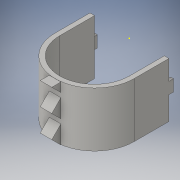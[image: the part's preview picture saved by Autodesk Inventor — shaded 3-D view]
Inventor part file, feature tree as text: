
AUTODESK INVENTOR PART (.ipt)
format: ipt  version: 2016 (Build 200138000, 138)  size: 207,360 bytes
history: native  units: in
note: dims shown in document units (in); Inventor stores cm internally (conversion verified against a paired STEP export)
features: sketch x8, extrude x7, reference x6, plane x1
ambient origin geometry x8: Origin, YZ Plane, XZ Plane, XY Plane, X Axis, Y Axis, Z Axis, Center Point
bodies: Solid1 (feature_tree)
feature tree (22):
  extrude  "Extrusion1"  Depth=1.5in TaperAngle=0.0deg
  extrude  "Extrusion2"  Depth=0.1969in TaperAngle=0.0deg
  extrude  "Extrusion3"  [1 undecoded]
  extrude  "Extrusion4"  Depth=0.3937in
  plane  "Work Plane1"
  sketch  "Sketch5"  dims[d12=1.9685in d14=0.9774in d15=0.3937in d17=1.0in d19=0.5in d20=0.0in]
  extrude  "Extrusion5"  Depth=0.5in TaperAngle=0.0deg
  extrude  "Extrusion6"  Depth=0.197in TaperAngle=0.0deg
  extrude  "Extrusion7"  [1 undecoded]
  sketch  "Sketch1"  dims[d0=0.1969in d1=1.5in d2=0.0in]
  reference  "Reference1"
  sketch  "Sketch2"  dims[d3=4.6969in d4=0.0in d5=0.1969in d6=0.0in]
  sketch  "Sketch3"  dims[d7=0.1969in d8=0.0in d9=-1.697in]
  sketch  "Sketch4"  dims[d10=0.7874in d11=0.3937in]
  reference  "Reference2"
  sketch  "Sketch6"  dims[d21=0.197in d22=0.0in d23=100.0in d24=0.0in]
  sketch  "Sketch8"
  reference  "Reference3"
  reference  "Reference4"
  reference  "Reference5"
  reference  "Reference6"
  sketch  "Sketch9"
note: 2 required parameter values undecoded (feature->parameter linkage not recoverable at this tier; creation-order binding heuristic only, values carry confidence <= 0.55)
